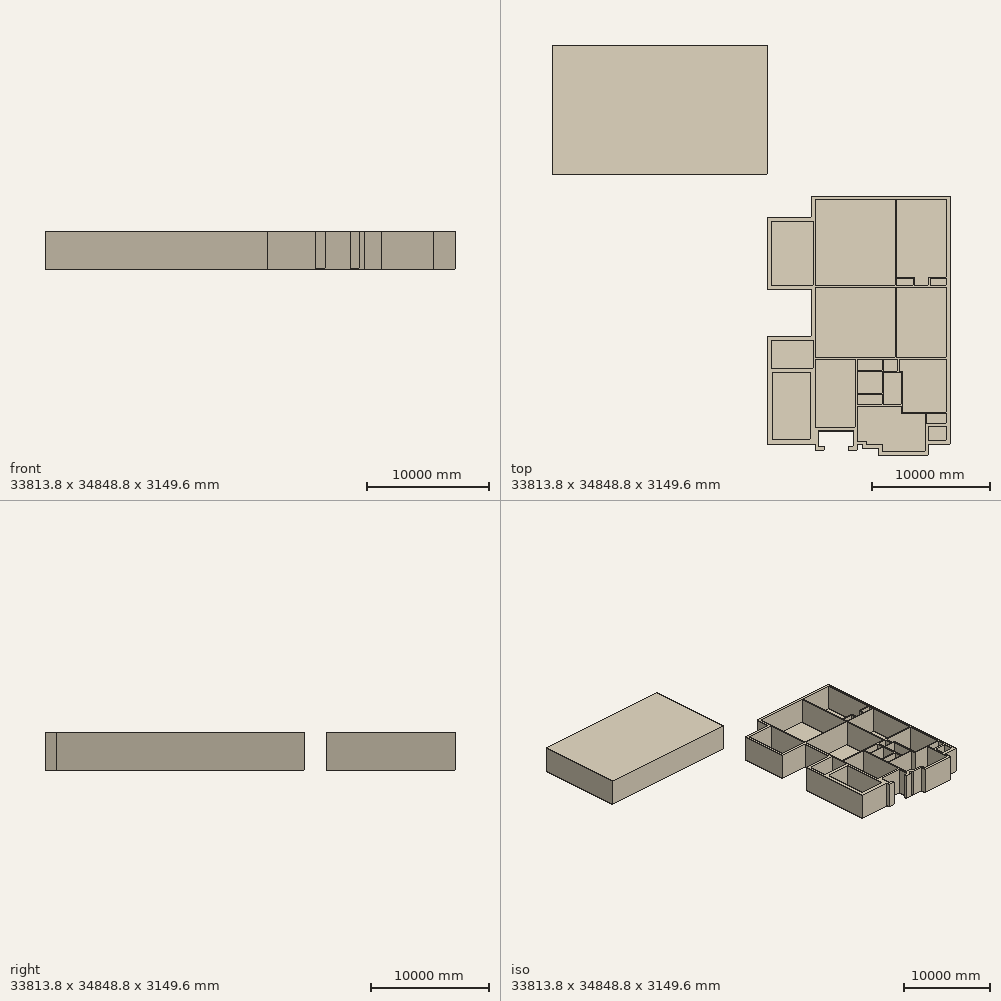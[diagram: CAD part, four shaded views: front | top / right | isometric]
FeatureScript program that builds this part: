
annotation { "Feature Type Name" : "Feature", "Feature Type Description" : "" }
export const myFeature = defineFeature(function(context is Context, id is Id, definition is map)
    precondition{}
    {
        {
            var Q0;
            Q0=qCreatedBy(makeId("Top.planeOp"),FACE);
            var sketch = newSketch(context, id + "F0", { "sketchPlane" : qUnion([Q0])});
            skLineSegment(sketch, "E0.bottom", {"start": v(3714.75, 0) * mm, "end": v(15525.75, 0) * mm});
            skLineSegment(sketch, "E0.right", {"start": v(15525.75, 0) * mm, "end": v(15525.75, -21132.8) * mm});
            skLineSegment(sketch, "E1", {"start": v(13696.95, -21132.8) * mm, "end": v(13696.95, -22047.2) * mm});
            skLineSegment(sketch, "E2", {"start": v(13696.95, -22047.2) * mm, "end": v(9429.75, -22047.2) * mm});
            skLineSegment(sketch, "E3", {"start": v(9429.75, -22047.2) * mm, "end": v(9429.75, -21437.6) * mm});
            skLineSegment(sketch, "E4", {"start": v(9429.75, -21437.6) * mm, "end": v(8058.15, -21437.6) * mm});
            skLineSegment(sketch, "E5", {"start": v(8058.15, -21437.6) * mm, "end": v(8058.15, -21132.8) * mm});
            skLineSegment(sketch, "E6.trimOffspring", {"start": v(13696.95, -21132.8) * mm, "end": v(15525.75, -21132.8) * mm});
            skLineSegment(sketch, "E7", {"start": v(7600.95, -21132.8) * mm, "end": v(7600.95, -21590) * mm});
            skLineSegment(sketch, "E8", {"start": v(7600.95, -21590) * mm, "end": v(6838.95, -21590) * mm});
            skLineSegment(sketch, "E9", {"start": v(4019.55, -21590) * mm, "end": v(4019.55, -21132.8) * mm});
            skLineSegment(sketch, "E10.trimOffspring", {"start": v(7600.95, -21132.8) * mm, "end": v(8058.15, -21132.8) * mm});
            skLineSegment(sketch, "E11", {"start": v(4781.55, -21590) * mm, "end": v(4781.55, -21285.2) * mm});
            skLineSegment(sketch, "E12", {"start": v(4781.55, -21285.2) * mm, "end": v(4324.35, -21285.2) * mm});
            skLineSegment(sketch, "E13", {"start": v(4324.35, -21285.2) * mm, "end": v(4324.35, -19964.4) * mm});
            skLineSegment(sketch, "E14", {"start": v(4324.35, -19964.4) * mm, "end": v(7296.15, -19964.4) * mm});
            skLineSegment(sketch, "E15", {"start": v(7296.15, -19964.4) * mm, "end": v(7296.15, -21285.2) * mm});
            skLineSegment(sketch, "E16", {"start": v(7296.15, -21285.2) * mm, "end": v(6838.95, -21285.2) * mm});
            skLineSegment(sketch, "E17", {"start": v(6838.95, -21285.2) * mm, "end": v(6838.95, -21590) * mm});
            skLineSegment(sketch, "E18.trimOffspring", {"start": v(4781.55, -21590) * mm, "end": v(4019.55, -21590) * mm});
            skLineSegment(sketch, "E19", {"start": v(4019.55, -304.8) * mm, "end": v(15220.95, -304.8) * mm});
            skLineSegment(sketch, "E20", {"start": v(15220.95, -304.8) * mm, "end": v(15220.95, -19310.35) * mm});
            skLineSegment(sketch, "E21", {"start": v(15430.5, -21037.55) * mm, "end": v(13392.15, -21037.55) * mm});
            skLineSegment(sketch, "E22", {"start": v(13392.15, -21037.55) * mm, "end": v(13392.15, -21742.4) * mm});
            skLineSegment(sketch, "E23", {"start": v(13392.15, -21742.4) * mm, "end": v(9734.55, -21742.4) * mm});
            skLineSegment(sketch, "E24", {"start": v(9734.55, -21742.4) * mm, "end": v(9734.55, -21132.8) * mm});
            skLineSegment(sketch, "E25", {"start": v(8362.95, -20828) * mm, "end": v(7600.95, -20828) * mm});
            skLineSegment(sketch, "E26", {"start": v(4019.55, -19659.6) * mm, "end": v(7600.95, -19659.6) * mm});
            skLineSegment(sketch, "E27", {"start": v(7600.95, -19659.6) * mm, "end": v(7600.95, -20828) * mm});
            skLineSegment(sketch, "E28", {"start": v(8362.95, -20828) * mm, "end": v(8362.95, -21132.8) * mm});
            skLineSegment(sketch, "E29", {"start": v(8362.95, -21132.8) * mm, "end": v(9734.55, -21132.8) * mm});
            skLineSegment(sketch, "E30", {"start": v(4019.55, -13868.4) * mm, "end": v(4019.55, -304.8) * mm});
            skLineSegment(sketch, "E31", {"start": v(4019.55, -13868.4) * mm, "end": v(15220.95, -13868.4) * mm});
            skLineSegment(sketch, "E32", {"start": v(4019.55, -13754.1) * mm, "end": v(15220.95, -13754.1) * mm});
            skLineSegment(sketch, "E33", {"start": v(7600.95, -19659.6) * mm, "end": v(7600.95, -13868.4) * mm});
            skLineSegment(sketch, "E34", {"start": v(7486.65, -19659.6) * mm, "end": v(7486.65, -13868.4) * mm});
            skLineSegment(sketch, "E35", {"start": v(7600.95, -17741.9) * mm, "end": v(11372.85, -17741.9) * mm});
            skLineSegment(sketch, "E36", {"start": v(7600.95, -17856.2) * mm, "end": v(11487.15, -17856.2) * mm});
            skLineSegment(sketch, "E37", {"start": v(9848.85, -17741.9) * mm, "end": v(9848.85, -13868.4) * mm});
            skLineSegment(sketch, "E38", {"start": v(9734.55, -17741.9) * mm, "end": v(9734.55, -13868.4) * mm});
            skLineSegment(sketch, "E39", {"start": v(9848.85, -14998.7) * mm, "end": v(11372.85, -14998.7) * mm});
            skLineSegment(sketch, "E40", {"start": v(11372.85, -14998.7) * mm, "end": v(11372.85, -17741.9) * mm});
            skLineSegment(sketch, "E41", {"start": v(9848.85, -14884.4) * mm, "end": v(11487.15, -14884.4) * mm});
            skLineSegment(sketch, "E42", {"start": v(11487.15, -14884.4) * mm, "end": v(11487.15, -17856.2) * mm});
            skLineSegment(sketch, "E43", {"start": v(7600.95, -14782.8) * mm, "end": v(9734.55, -14782.8) * mm});
            skLineSegment(sketch, "E44", {"start": v(7600.95, -14897.1) * mm, "end": v(9734.55, -14897.1) * mm});
            skLineSegment(sketch, "E45", {"start": v(7600.95, -16852.9) * mm, "end": v(9734.55, -16852.9) * mm});
            skLineSegment(sketch, "E46", {"start": v(7600.95, -16738.6) * mm, "end": v(9734.55, -16738.6) * mm});
            skLineSegment(sketch, "E47", {"start": v(9124.95, -14897.1) * mm, "end": v(9124.95, -16738.6) * mm});
            skLineSegment(sketch, "E48", {"start": v(8515.35, -13868.4) * mm, "end": v(8515.35, -14782.8) * mm});
            skLineSegment(sketch, "E49", {"start": v(9848.85, -16929.1) * mm, "end": v(11372.85, -16929.1) * mm});
            skLineSegment(sketch, "E50.bottom", {"start": v(9455.15, -17043.4) * mm, "end": v(9683.75, -17043.4) * mm});
            skLineSegment(sketch, "E50.top", {"start": v(9455.15, -17551.4) * mm, "end": v(9683.75, -17551.4) * mm});
            skLineSegment(sketch, "E50.left", {"start": v(9455.15, -17043.4) * mm, "end": v(9455.15, -17551.4) * mm});
            skLineSegment(sketch, "E50.right", {"start": v(9683.75, -17043.4) * mm, "end": v(9683.75, -17551.4) * mm});
            skEllipse(sketch, "E51", {"center": v(9201.15, -17297.4) * mm, "majorRadius": 266.7 * mm, "minorRadius": 152.4 * mm, "majorAxis": v(1, 0)});
            skLineSegment(sketch, "E52", {"start": v(9683.75, -17043.4) * mm, "end": v(9683.75, -16852.9) * mm, "construction": true});
            skLineSegment(sketch, "E53", {"start": v(9683.75, -17551.4) * mm, "end": v(9683.75, -17741.9) * mm, "construction": true});
            skLineSegment(sketch, "E54", {"start": v(8934.45, -17297.4) * mm, "end": v(9455.15, -17297.4) * mm});
            skLineSegment(sketch, "E55.bottom", {"start": v(11093.45, -16319.5) * mm, "end": v(11322.05, -16319.5) * mm});
            skLineSegment(sketch, "E55.top", {"start": v(11093.45, -16827.5) * mm, "end": v(11322.05, -16827.5) * mm});
            skLineSegment(sketch, "E55.left", {"start": v(11093.45, -16319.5) * mm, "end": v(11093.45, -16827.5) * mm});
            skLineSegment(sketch, "E55.right", {"start": v(11322.05, -16319.5) * mm, "end": v(11322.05, -16827.5) * mm});
            skEllipse(sketch, "E56", {"center": v(10839.45, -16573.5) * mm, "majorRadius": 266.7 * mm, "minorRadius": 152.4 * mm, "majorAxis": v(1, 0)});
            skLineSegment(sketch, "E57", {"start": v(10572.75, -16573.5) * mm, "end": v(11093.45, -16573.5) * mm});
            skLineSegment(sketch, "E58", {"start": v(10763.25, -14998.7) * mm, "end": v(10763.25, -16217.9) * mm});
            skLineSegment(sketch, "E59", {"start": v(10763.25, -16217.9) * mm, "end": v(11372.85, -16217.9) * mm});
            skLineSegment(sketch, "E60", {"start": v(11182.35, -14884.4) * mm, "end": v(11182.35, -13868.4) * mm});
            skLineSegment(sketch, "E61", {"start": v(11068.05, -14884.4) * mm, "end": v(11068.05, -13868.4) * mm});
            skLineSegment(sketch, "E62", {"start": v(11068.05, -14808.2) * mm, "end": v(11182.35, -14808.2) * mm});
            skLineSegment(sketch, "E63", {"start": v(9848.85, -13754.1) * mm, "end": v(9848.85, -13868.4) * mm});
            skLineSegment(sketch, "E64", {"start": v(11068.05, -13944.6) * mm, "end": v(11182.35, -13944.6) * mm});
            skLineSegment(sketch, "E65.bottom", {"start": v(12731.75, -13893.8) * mm, "end": v(14763.75, -13893.8) * mm});
            skLineSegment(sketch, "E65.top", {"start": v(12731.75, -16103.6) * mm, "end": v(14763.75, -16103.6) * mm});
            skLineSegment(sketch, "E65.left", {"start": v(12731.75, -13893.8) * mm, "end": v(12731.75, -16103.6) * mm});
            skLineSegment(sketch, "E65.right", {"start": v(14763.75, -13893.8) * mm, "end": v(14763.75, -16103.6) * mm});
            skLineSegment(sketch, "E66", {"start": v(11372.85, -17741.9) * mm, "end": v(11372.85, -18465.8) * mm});
            skLineSegment(sketch, "E67", {"start": v(11372.85, -18465.8) * mm, "end": v(15220.95, -18465.8) * mm});
            skLineSegment(sketch, "E68", {"start": v(11487.15, -17856.2) * mm, "end": v(11487.15, -18351.5) * mm});
            skLineSegment(sketch, "E69", {"start": v(11487.15, -18351.5) * mm, "end": v(15220.95, -18351.5) * mm});
            skLineSegment(sketch, "E70", {"start": v(13392.15, -19310.35) * mm, "end": v(15220.95, -19310.35) * mm});
            skLineSegment(sketch, "E71", {"start": v(15430.5, -19310.35) * mm, "end": v(15430.5, -21037.55) * mm});
            skLineSegment(sketch, "E72", {"start": v(13392.15, -21037.55) * mm, "end": v(13392.15, -19310.35) * mm});
            skLineSegment(sketch, "E73", {"start": v(15220.95, -19310.35) * mm, "end": v(15430.5, -19310.35) * mm});
            skLineSegment(sketch, "E74.bottom", {"start": v(13671.55, -19589.75) * mm, "end": v(15151.1, -19589.75) * mm});
            skLineSegment(sketch, "E74.top", {"start": v(13671.55, -20758.15) * mm, "end": v(15151.1, -20758.15) * mm});
            skLineSegment(sketch, "E74.left", {"start": v(13671.55, -19589.75) * mm, "end": v(13671.55, -20758.15) * mm});
            skLineSegment(sketch, "E74.right", {"start": v(15151.1, -19589.75) * mm, "end": v(15151.1, -20758.15) * mm});
            skLineSegment(sketch, "E75", {"start": v(13392.15, -19310.35) * mm, "end": v(13392.15, -18465.8) * mm});
            skLineSegment(sketch, "E76", {"start": v(13506.45, -19310.35) * mm, "end": v(13506.45, -18465.8) * mm});
            skLineSegment(sketch, "E77", {"start": v(4019.55, -7620) * mm, "end": v(15220.95, -7620) * mm});
            skLineSegment(sketch, "E78", {"start": v(10839.45, -304.8) * mm, "end": v(10839.45, -7620) * mm});
            skLineSegment(sketch, "E79", {"start": v(10953.75, -304.8) * mm, "end": v(10953.75, -7620) * mm});
            skLineSegment(sketch, "E80", {"start": v(4019.55, -7734.3) * mm, "end": v(15220.95, -7734.3) * mm});
            skLineSegment(sketch, "E81", {"start": v(10839.45, -13754.1) * mm, "end": v(10839.45, -7734.3) * mm});
            skLineSegment(sketch, "E82", {"start": v(10953.75, -7734.3) * mm, "end": v(10953.75, -13754.1) * mm});
            skLineSegment(sketch, "E83", {"start": v(13747.75, -18351.5) * mm, "end": v(13747.75, -18465.8) * mm});
            skLineSegment(sketch, "E84", {"start": v(14966.95, -18351.5) * mm, "end": v(14966.95, -18465.8) * mm});
            skLineSegment(sketch, "E85.bottom", {"start": v(11512.55, -17335.5) * mm, "end": v(13417.55, -17335.5) * mm});
            skLineSegment(sketch, "E85.top", {"start": v(11512.55, -18326.1) * mm, "end": v(13417.55, -18326.1) * mm});
            skLineSegment(sketch, "E85.left", {"start": v(11512.55, -17335.5) * mm, "end": v(11512.55, -18326.1) * mm});
            skLineSegment(sketch, "E85.right", {"start": v(13417.55, -17335.5) * mm, "end": v(13417.55, -18326.1) * mm});
            skLineSegment(sketch, "E86", {"start": v(10953.75, -7010.4) * mm, "end": v(12490.45, -7010.4) * mm});
            skLineSegment(sketch, "E87", {"start": v(10953.75, -6896.1) * mm, "end": v(12490.45, -6896.1) * mm});
            skLineSegment(sketch, "E88", {"start": v(12490.45, -6896.1) * mm, "end": v(12490.45, -7734.3) * mm});
            skLineSegment(sketch, "E89", {"start": v(12376.15, -6896.1) * mm, "end": v(12376.15, -7734.3) * mm});
            skLineSegment(sketch, "E90", {"start": v(13684.25, -6896.1) * mm, "end": v(13684.25, -7734.3) * mm});
            skLineSegment(sketch, "E91", {"start": v(13798.55, -6896.1) * mm, "end": v(13798.55, -7734.3) * mm});
            skLineSegment(sketch, "E92.trimOffspring", {"start": v(13684.25, -7010.4) * mm, "end": v(15220.95, -7010.4) * mm});
            skLineSegment(sketch, "E93.trimOffspring", {"start": v(13684.25, -6896.1) * mm, "end": v(15220.95, -6896.1) * mm});
            skLineSegment(sketch, "E94.bottom", {"start": v(0, -14674.85) * mm, "end": v(4019.55, -14674.85) * mm});
            skLineSegment(sketch, "E94.top", {"start": v(0, -21132.8) * mm, "end": v(4019.55, -21132.8) * mm});
            skLineSegment(sketch, "E94.left", {"start": v(0, -14674.85) * mm, "end": v(0, -21132.8) * mm});
            skLineSegment(sketch, "E94.right", {"start": v(4019.55, -14674.85) * mm, "end": v(4019.55, -21132.8) * mm});
            skLineSegment(sketch, "E95.bottom", {"start": v(438.15, -15030.45) * mm, "end": v(3663.95, -15030.45) * mm});
            skLineSegment(sketch, "E95.top", {"start": v(438.15, -20694.65) * mm, "end": v(3663.95, -20694.65) * mm});
            skLineSegment(sketch, "E95.left", {"start": v(438.15, -15030.45) * mm, "end": v(438.15, -20694.65) * mm});
            skLineSegment(sketch, "E95.right", {"start": v(3663.95, -15030.45) * mm, "end": v(3663.95, -20694.65) * mm});
            skLineSegment(sketch, "E96.bottom", {"start": v(3905.25, -2133.6) * mm, "end": v(304.8, -2133.6) * mm});
            skLineSegment(sketch, "E96.top", {"start": v(3905.25, -7620) * mm, "end": v(304.8, -7620) * mm});
            skLineSegment(sketch, "E96.left", {"start": v(3905.25, -2133.6) * mm, "end": v(3905.25, -7620) * mm});
            skLineSegment(sketch, "E96.right", {"start": v(304.8, -2133.6) * mm, "end": v(304.8, -7620) * mm});
            skLineSegment(sketch, "E97", {"start": v(3714.75, 0) * mm, "end": v(3714.75, -1828.8) * mm});
            skLineSegment(sketch, "E98", {"start": v(3714.75, -1828.8) * mm, "end": v(0, -1828.8) * mm});
            skLineSegment(sketch, "E99", {"start": v(0, -1828.8) * mm, "end": v(0, -7924.8) * mm});
            skLineSegment(sketch, "E100", {"start": v(4019.55, -14674.85) * mm, "end": v(4019.55, -13868.4) * mm});
            skLineSegment(sketch, "E101", {"start": v(0, -7924.8) * mm, "end": v(3714.75, -7924.8) * mm});
            skLineSegment(sketch, "E102", {"start": v(3714.75, -7924.8) * mm, "end": v(3714.75, -11931.65) * mm});
            skLineSegment(sketch, "E103", {"start": v(3714.75, -11931.65) * mm, "end": v(0, -11931.65) * mm});
            skLineSegment(sketch, "E104", {"start": v(0, -11931.65) * mm, "end": v(0, -14674.85) * mm});
            skLineSegment(sketch, "E105", {"start": v(304.8, -14674.85) * mm, "end": v(304.8, -12236.45) * mm});
            skLineSegment(sketch, "E106", {"start": v(304.8, -12236.45) * mm, "end": v(3905.25, -12236.45) * mm});
            skLineSegment(sketch, "E107", {"start": v(3905.25, -12236.45) * mm, "end": v(3905.25, -14674.85) * mm});
            skLineSegment(sketch, "E108.bottom", {"start": v(-18288, 12801.6) * mm, "end": v(0, 12801.6) * mm});
            skLineSegment(sketch, "E108.top", {"start": v(-18288, 1828.8) * mm, "end": v(0, 1828.8) * mm});
            skLineSegment(sketch, "E108.left", {"start": v(-18288, 12801.6) * mm, "end": v(-18288, 1828.8) * mm});
            skLineSegment(sketch, "E108.right", {"start": v(0, 12801.6) * mm, "end": v(0, 1828.8) * mm});
            skLineSegment(sketch, "E109", {"start": v(-12192, 12801.6) * mm, "end": v(-12192, 1828.8) * mm});
            skLineSegment(sketch, "E110", {"start": v(-3048, 12801.6) * mm, "end": v(-3048, 1828.8) * mm});
            skSolve(sketch);
        }
        {
            var Q0;
            Q0=qCreatedBy(makeId("Top.planeOp"),FACE);
            var sketch = newSketch(context, id + "F1", { "sketchPlane" : qUnion([Q0])});
            skLineSegment(sketch, "E111.0", {"start": v(0, -11931.65) * mm, "end": v(0, -21132.8) * mm});
            skLineSegment(sketch, "E112.0", {"start": v(3714.75, -11931.65) * mm, "end": v(0, -11931.65) * mm});
            skLineSegment(sketch, "E113.0", {"start": v(3714.75, -7924.8) * mm, "end": v(3714.75, -11931.65) * mm});
            skLineSegment(sketch, "E114.0", {"start": v(0, -7924.8) * mm, "end": v(3714.75, -7924.8) * mm});
            skLineSegment(sketch, "E115.0", {"start": v(0, -1828.8) * mm, "end": v(0, -7924.8) * mm});
            skLineSegment(sketch, "E116.0", {"start": v(3714.75, -1828.8) * mm, "end": v(0, -1828.8) * mm});
            skLineSegment(sketch, "E117.0", {"start": v(3714.75, 0) * mm, "end": v(3714.75, -1828.8) * mm});
            skLineSegment(sketch, "E118.0", {"start": v(3714.75, 0) * mm, "end": v(15525.75, 0) * mm});
            skLineSegment(sketch, "E119.0", {"start": v(15525.75, 0) * mm, "end": v(15525.75, -21132.8) * mm});
            skLineSegment(sketch, "E120.0", {"start": v(13696.95, -21132.8) * mm, "end": v(15525.75, -21132.8) * mm});
            skLineSegment(sketch, "E121.0", {"start": v(13696.95, -21132.8) * mm, "end": v(13696.95, -22047.2) * mm});
            skLineSegment(sketch, "E122.0", {"start": v(13696.95, -22047.2) * mm, "end": v(9429.75, -22047.2) * mm});
            skLineSegment(sketch, "E123.0", {"start": v(9429.75, -22047.2) * mm, "end": v(9429.75, -21437.6) * mm});
            skLineSegment(sketch, "E124.0", {"start": v(9429.75, -21437.6) * mm, "end": v(8058.15, -21437.6) * mm});
            skLineSegment(sketch, "E125.0", {"start": v(8058.15, -21437.6) * mm, "end": v(8058.15, -21132.8) * mm});
            skLineSegment(sketch, "E126.0", {"start": v(7296.15, -19964.4) * mm, "end": v(7296.15, -21132.8) * mm});
            skLineSegment(sketch, "E127.0", {"start": v(4324.35, -19964.4) * mm, "end": v(7296.15, -19964.4) * mm});
            skLineSegment(sketch, "E128.0", {"start": v(4324.35, -21132.8) * mm, "end": v(4324.35, -19964.4) * mm});
            skLineSegment(sketch, "E129.0", {"start": v(0, -21132.8) * mm, "end": v(4324.35, -21132.8) * mm});
            skLineSegment(sketch, "E130", {"start": v(8058.15, -21132.8) * mm, "end": v(7296.15, -21132.8) * mm});
            skSolve(sketch);
        }
        {
            var Q0;
            Q0 = qSketchRegion(id + "F1", true);
            var Q1;
            {var subQ0=sQuery(id+"F0.wireOp",EDGE,"E108.left");Q1=makeQuery(id+"F0.imprint","IMPRINT",FACE,{"disambiguationData":[TD([[makeQuery(id+"F0.imprint","IMPRINT",EDGE,{"derivedFrom":subQ0}),1.0]])]});}
            var Q2;
            {var subQ0=sQuery(id+"F0.wireOp",EDGE,"E109");Q2=makeQuery(id+"F0.imprint","IMPRINT",FACE,{"disambiguationData":[TD([[makeQuery(id+"F0.imprint","IMPRINT",EDGE,{"derivedFrom":subQ0}),1.0]])]});}
            var Q3;
            {var subQ0=sQuery(id+"F0.wireOp",EDGE,"E108.right");Q3=makeQuery(id+"F0.imprint","IMPRINT",FACE,{"disambiguationData":[TD([[makeQuery(id+"F0.imprint","IMPRINT",EDGE,{"derivedFrom":subQ0}),-1.0]])]});}
            extrude(context, id + "F2", {"entities" : qUnion([Q0, Q1, Q2, Q3]), "oppositeDirection" : true, "depth" : 101.6 * mm, "offsetDistance" : 25.4 * mm});
        }
        {
            var Q0;
            Q0=makeQuery(id+"F0.imprint","IMPRINT",FACE,{"disambiguationData":[TD([[makeQuery(id+"F0.imprint","IMPRINT",EDGE,{"derivedFrom":sQuery(id+"F0.wireOp",EDGE,"E0.bottom")}),-1.0]])]});
            var Q1;
            {var subQ1=sQuery(id+"F0.wireOp",EDGE,"E94.top");Q1=makeQuery(id+"F0.imprint","IMPRINT",FACE,{"disambiguationData":[TD([[makeQuery(id+"F0.imprint","IMPRINT",EDGE,{"derivedFrom":subQ1}),1.0]])]});}
            var Q2;
            {var subQ0=sQuery(id+"F0.wireOp",EDGE,"E78");Q2=makeQuery(id+"F0.imprint","IMPRINT",FACE,{"disambiguationData":[TD([[makeQuery(id+"F0.imprint","IMPRINT",EDGE,{"derivedFrom":subQ0}),1.0]])]});}
            var Q3;
            {var subQ0=sQuery(id+"F0.wireOp",EDGE,"E77");var subQ7=sQuery(id+"F0.wireOp",EDGE,"E30");var subQ8=makeQuery(id+"F0.imprint","INTERSECT",VERTEX,{"derivedFrom":[subQ7,subQ0]});Q3=makeQuery(id+"F0.imprint","IMPRINT",FACE,{"disambiguationData":[TD([[makeQuery(id+"F0.imprint","IMPRINT",EDGE,{"disambiguationData":[TD([[subQ8,1.0]])],"derivedFrom":subQ7}),-1.0]])]});}
            var Q4;
            {var subQ0=sQuery(id+"F0.wireOp",EDGE,"E81");Q4=makeQuery(id+"F0.imprint","IMPRINT",FACE,{"disambiguationData":[TD([[makeQuery(id+"F0.imprint","IMPRINT",EDGE,{"derivedFrom":subQ0}),-1.0]])]});}
            var Q5;
            {var subQ0=sQuery(id+"F0.wireOp",EDGE,"E89");var subQ1=sQuery(id+"F0.wireOp",EDGE,"E77");var subQ2=makeQuery(id+"F0.imprint","INTERSECT",VERTEX,{"derivedFrom":[subQ1,subQ0]});Q5=makeQuery(id+"F0.imprint","IMPRINT",FACE,{"disambiguationData":[TD([[makeQuery(id+"F0.imprint","IMPRINT",EDGE,{"disambiguationData":[TD([[subQ2,-1.0]])],"derivedFrom":subQ1}),1.0]])]});}
            var Q6;
            {var subQ0=sQuery(id+"F0.wireOp",EDGE,"E86");var subQ1=sQuery(id+"F0.wireOp",EDGE,"E79");var subQ2=makeQuery(id+"F0.imprint","INTERSECT",VERTEX,{"derivedFrom":[subQ1,subQ0]});Q6=makeQuery(id+"F0.imprint","IMPRINT",FACE,{"disambiguationData":[TD([[makeQuery(id+"F0.imprint","IMPRINT",EDGE,{"disambiguationData":[TD([[subQ2,1.0]])],"derivedFrom":subQ1}),1.0]])]});}
            var Q7;
            {var subQ0=sQuery(id+"F0.wireOp",EDGE,"E88");var subQ1=sQuery(id+"F0.wireOp",EDGE,"E86");var subQ2=makeQuery(id+"F0.imprint","INTERSECT",VERTEX,{"derivedFrom":[subQ1,subQ0]});Q7=makeQuery(id+"F0.imprint","IMPRINT",FACE,{"disambiguationData":[TD([[makeQuery(id+"F0.imprint","IMPRINT",EDGE,{"disambiguationData":[TD([[subQ2,1.0]])],"derivedFrom":subQ1}),1.0]])]});}
            var Q8;
            {var subQ0=sQuery(id+"F0.wireOp",EDGE,"E89");var subQ1=sQuery(id+"F0.wireOp",EDGE,"E77");var subQ2=makeQuery(id+"F0.imprint","INTERSECT",VERTEX,{"derivedFrom":[subQ1,subQ0]});Q8=makeQuery(id+"F0.imprint","IMPRINT",FACE,{"disambiguationData":[TD([[makeQuery(id+"F0.imprint","IMPRINT",EDGE,{"disambiguationData":[TD([[subQ2,-1.0]])],"derivedFrom":subQ1}),-1.0]])]});}
            var Q9;
            {var subQ0=sQuery(id+"F0.wireOp",EDGE,"E88");var subQ1=sQuery(id+"F0.wireOp",EDGE,"E77");var subQ2=makeQuery(id+"F0.imprint","INTERSECT",VERTEX,{"derivedFrom":[subQ1,subQ0]});Q9=makeQuery(id+"F0.imprint","IMPRINT",FACE,{"disambiguationData":[TD([[makeQuery(id+"F0.imprint","IMPRINT",EDGE,{"disambiguationData":[TD([[subQ2,-1.0]])],"derivedFrom":subQ1}),-1.0]])]});}
            var Q10;
            {var subQ0=sQuery(id+"F0.wireOp",EDGE,"E92.trimOffspring");var subQ1=sQuery(id+"F0.wireOp",EDGE,"E20");var subQ2=makeQuery(id+"F0.imprint","INTERSECT",VERTEX,{"derivedFrom":[subQ1,subQ0]});Q10=makeQuery(id+"F0.imprint","IMPRINT",FACE,{"disambiguationData":[TD([[makeQuery(id+"F0.imprint","IMPRINT",EDGE,{"disambiguationData":[TD([[subQ2,1.0]])],"derivedFrom":subQ1}),-1.0]])]});}
            var Q11;
            {var subQ0=sQuery(id+"F0.wireOp",EDGE,"E93.trimOffspring");var subQ1=sQuery(id+"F0.wireOp",EDGE,"E90");var subQ2=makeQuery(id+"F0.imprint","INTERSECT",VERTEX,{"derivedFrom":[subQ1,subQ0]});Q11=makeQuery(id+"F0.imprint","IMPRINT",FACE,{"disambiguationData":[TD([[makeQuery(id+"F0.imprint","IMPRINT",EDGE,{"disambiguationData":[TD([[subQ2,-1.0]])],"derivedFrom":subQ1}),1.0]])]});}
            var Q12;
            {var subQ0=sQuery(id+"F0.wireOp",EDGE,"E90");var subQ1=sQuery(id+"F0.wireOp",EDGE,"E77");var subQ2=makeQuery(id+"F0.imprint","INTERSECT",VERTEX,{"derivedFrom":[subQ1,subQ0]});Q12=makeQuery(id+"F0.imprint","IMPRINT",FACE,{"disambiguationData":[TD([[makeQuery(id+"F0.imprint","IMPRINT",EDGE,{"disambiguationData":[TD([[subQ2,-1.0]])],"derivedFrom":subQ1}),1.0]])]});}
            var Q13;
            {var subQ0=sQuery(id+"F0.wireOp",EDGE,"E90");var subQ1=sQuery(id+"F0.wireOp",EDGE,"E77");var subQ2=makeQuery(id+"F0.imprint","INTERSECT",VERTEX,{"derivedFrom":[subQ1,subQ0]});Q13=makeQuery(id+"F0.imprint","IMPRINT",FACE,{"disambiguationData":[TD([[makeQuery(id+"F0.imprint","IMPRINT",EDGE,{"disambiguationData":[TD([[subQ2,-1.0]])],"derivedFrom":subQ1}),-1.0]])]});}
            var Q14;
            {var subQ0=sQuery(id+"F0.wireOp",EDGE,"E77");var subQ1=sQuery(id+"F0.wireOp",EDGE,"E20");var subQ2=makeQuery(id+"F0.imprint","INTERSECT",VERTEX,{"derivedFrom":[subQ1,subQ0]});Q14=makeQuery(id+"F0.imprint","IMPRINT",FACE,{"disambiguationData":[TD([[makeQuery(id+"F0.imprint","IMPRINT",EDGE,{"disambiguationData":[TD([[subQ2,-1.0]])],"derivedFrom":subQ1}),-1.0]])]});}
            var Q15;
            {var subQ3=sQuery(id+"F0.wireOp",EDGE,"E63");Q15=makeQuery(id+"F0.imprint","IMPRINT",FACE,{"disambiguationData":[TD([[makeQuery(id+"F0.imprint","IMPRINT",EDGE,{"derivedFrom":subQ3}),1.0]])]});}
            var Q16;
            {var subQ5=sQuery(id+"F0.wireOp",EDGE,"E64");Q16=makeQuery(id+"F0.imprint","IMPRINT",FACE,{"disambiguationData":[TD([[makeQuery(id+"F0.imprint","IMPRINT",EDGE,{"derivedFrom":subQ5}),1.0]])]});}
            var Q17;
            {var subQ5=sQuery(id+"F0.wireOp",EDGE,"E62");Q17=makeQuery(id+"F0.imprint","IMPRINT",FACE,{"disambiguationData":[TD([[makeQuery(id+"F0.imprint","IMPRINT",EDGE,{"derivedFrom":subQ5}),-1.0]])]});}
            var Q18;
            {var subQ0=sQuery(id+"F0.wireOp",EDGE,"E62");Q18=makeQuery(id+"F0.imprint","IMPRINT",FACE,{"disambiguationData":[TD([[makeQuery(id+"F0.imprint","IMPRINT",EDGE,{"derivedFrom":subQ0}),1.0]])]});}
            var Q19;
            {var subQ0=sQuery(id+"F0.wireOp",EDGE,"E42");Q19=makeQuery(id+"F0.imprint","IMPRINT",FACE,{"disambiguationData":[TD([[makeQuery(id+"F0.imprint","IMPRINT",EDGE,{"derivedFrom":subQ0}),-1.0]])]});}
            var Q20;
            {var subQ8=sQuery(id+"F0.wireOp",EDGE,"E63");Q20=makeQuery(id+"F0.imprint","IMPRINT",FACE,{"disambiguationData":[TD([[makeQuery(id+"F0.imprint","IMPRINT",EDGE,{"derivedFrom":subQ8}),-1.0]])]});}
            var Q21;
            {var subQ5=sQuery(id+"F0.wireOp",EDGE,"E34");Q21=makeQuery(id+"F0.imprint","IMPRINT",FACE,{"disambiguationData":[TD([[makeQuery(id+"F0.imprint","IMPRINT",EDGE,{"derivedFrom":subQ5}),-1.0]])]});}
            var Q22;
            {var subQ0=sQuery(id+"F0.wireOp",EDGE,"E43");var subQ4=sQuery(id+"F0.wireOp",EDGE,"E33");var subQ5=makeQuery(id+"F0.imprint","INTERSECT",VERTEX,{"derivedFrom":[subQ4,subQ0]});Q22=makeQuery(id+"F0.imprint","IMPRINT",FACE,{"disambiguationData":[TD([[makeQuery(id+"F0.imprint","IMPRINT",EDGE,{"disambiguationData":[TD([[subQ5,1.0]])],"derivedFrom":subQ4}),-1.0]])]});}
            var Q23;
            {var subQ4=sQuery(id+"F0.wireOp",EDGE,"E45");Q23=makeQuery(id+"F0.imprint","IMPRINT",FACE,{"disambiguationData":[TD([[makeQuery(id+"F0.imprint","IMPRINT",EDGE,{"derivedFrom":subQ4}),1.0]])]});}
            var Q24;
            {var subQ1=sQuery(id+"F0.wireOp",EDGE,"E35");var subQ5=sQuery(id+"F0.wireOp",EDGE,"E33");var subQ6=makeQuery(id+"F0.imprint","INTERSECT",VERTEX,{"derivedFrom":[subQ5,subQ1]});Q24=makeQuery(id+"F0.imprint","IMPRINT",FACE,{"disambiguationData":[TD([[makeQuery(id+"F0.imprint","IMPRINT",EDGE,{"disambiguationData":[TD([[subQ6,1.0]])],"derivedFrom":subQ5}),-1.0]])]});}
            var Q25;
            {var subQ4=sQuery(id+"F0.wireOp",EDGE,"E35");var subQ6=sQuery(id+"F0.wireOp",EDGE,"E37");var subQ13=makeQuery(id+"F0.imprint","INTERSECT",VERTEX,{"derivedFrom":[subQ4,subQ6]});Q25=makeQuery(id+"F0.imprint","IMPRINT",FACE,{"disambiguationData":[TD([[makeQuery(id+"F0.imprint","IMPRINT",EDGE,{"disambiguationData":[TD([[subQ13,1.0]])],"derivedFrom":subQ4}),1.0]])]});}
            var Q26;
            {var subQ7=sQuery(id+"F0.wireOp",EDGE,"E68");Q26=makeQuery(id+"F0.imprint","IMPRINT",FACE,{"disambiguationData":[TD([[makeQuery(id+"F0.imprint","IMPRINT",EDGE,{"derivedFrom":subQ7}),-1.0]])]});}
            var Q27;
            {var subQ5=sQuery(id+"F0.wireOp",EDGE,"E84");Q27=makeQuery(id+"F0.imprint","IMPRINT",FACE,{"disambiguationData":[TD([[makeQuery(id+"F0.imprint","IMPRINT",EDGE,{"derivedFrom":subQ5}),1.0]])]});}
            var Q28;
            {var subQ0=sQuery(id+"F0.wireOp",EDGE,"E83");Q28=makeQuery(id+"F0.imprint","IMPRINT",FACE,{"disambiguationData":[TD([[makeQuery(id+"F0.imprint","IMPRINT",EDGE,{"derivedFrom":subQ0}),1.0]])]});}
            var Q29;
            {var subQ0=sQuery(id+"F0.wireOp",EDGE,"E75");Q29=makeQuery(id+"F0.imprint","IMPRINT",FACE,{"disambiguationData":[TD([[makeQuery(id+"F0.imprint","IMPRINT",EDGE,{"derivedFrom":subQ0}),-1.0]])]});}
            var Q30;
            Q30=makeQuery(id+"F0.imprint","IMPRINT",FACE,{"disambiguationData":[TD([[makeQuery(id+"F0.imprint","IMPRINT",EDGE,{"derivedFrom":sQuery(id+"F0.wireOp",EDGE,"E21")}),-1.0]])]});
            var Q31;
            {var subQ0=sQuery(id+"F0.wireOp",EDGE,"E109");Q31=makeQuery(id+"F0.imprint","IMPRINT",FACE,{"disambiguationData":[TD([[makeQuery(id+"F0.imprint","IMPRINT",EDGE,{"derivedFrom":subQ0}),1.0]])]});}
            var Q32;
            {var subQ0=sQuery(id+"F0.wireOp",EDGE,"E108.right");Q32=makeQuery(id+"F0.imprint","IMPRINT",FACE,{"disambiguationData":[TD([[makeQuery(id+"F0.imprint","IMPRINT",EDGE,{"derivedFrom":subQ0}),-1.0]])]});}
            var Q33;
            {var subQ0=sQuery(id+"F0.wireOp",EDGE,"E108.left");Q33=makeQuery(id+"F0.imprint","IMPRINT",FACE,{"disambiguationData":[TD([[makeQuery(id+"F0.imprint","IMPRINT",EDGE,{"derivedFrom":subQ0}),1.0]])]});}
            extrude(context, id + "F3", {"entities" : qUnion([Q0, Q1, Q2, Q3, Q4, Q5, Q6, Q7, Q8, Q9, Q10, Q11, Q12, Q13, Q14, Q15, Q16, Q17, Q18, Q19, Q20, Q21, Q22, Q23, Q24, Q25, Q26, Q27, Q28, Q29, Q30, Q31, Q32, Q33]), "operationType" : NewBodyOperationType.ADD, "depth" : 3048 * mm, "offsetDistance" : 25.4 * mm});
        }
    });
